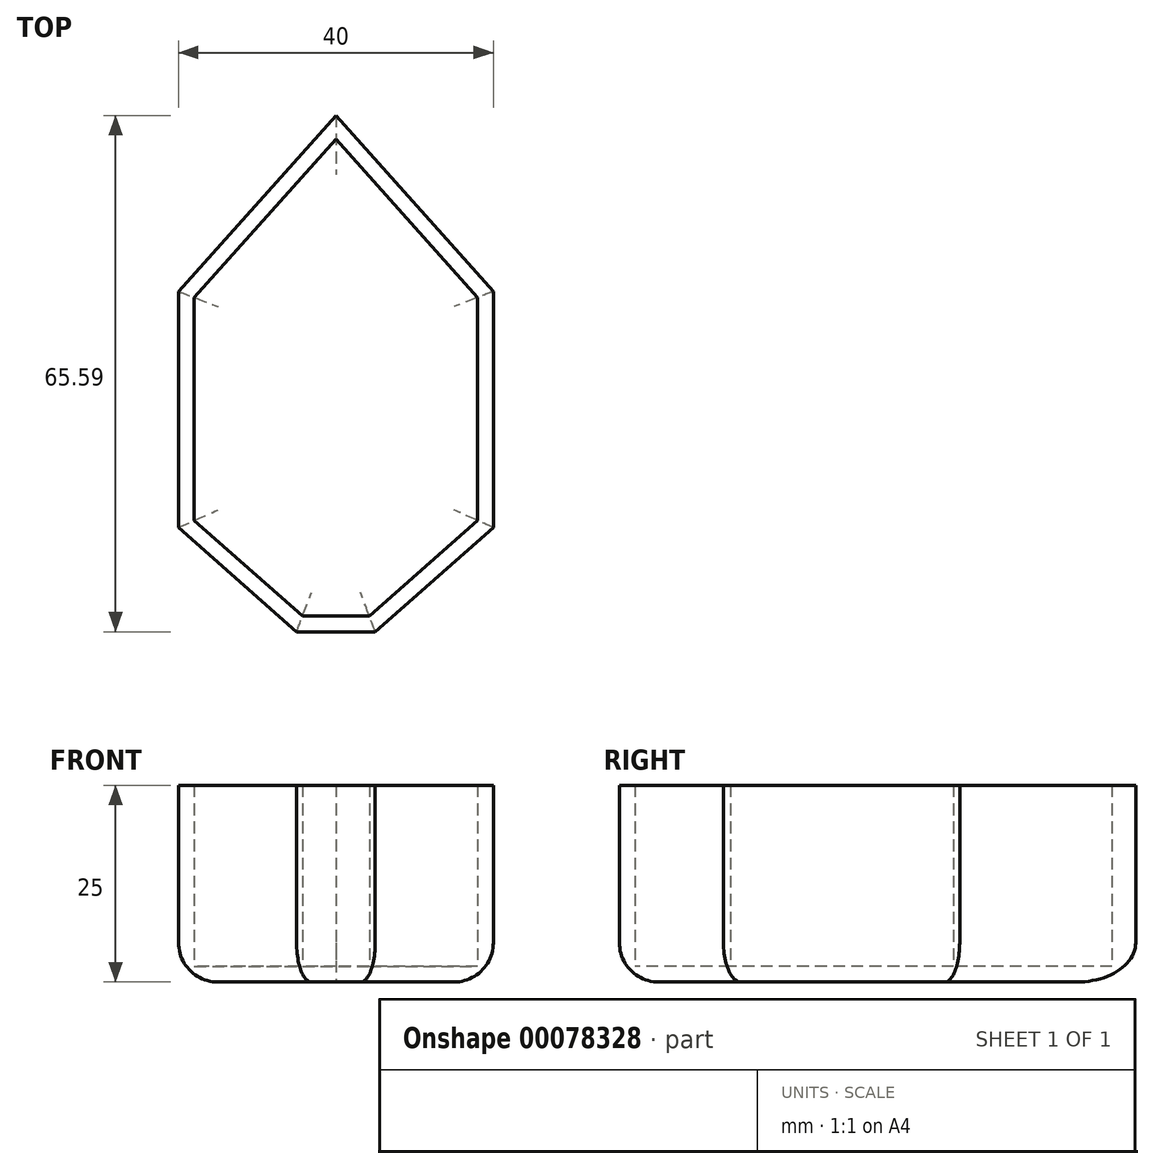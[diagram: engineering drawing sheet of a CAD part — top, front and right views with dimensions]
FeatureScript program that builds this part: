
annotation { "Feature Type Name" : "Feature", "Feature Type Description" : "" }
export const myFeature = defineFeature(function(context is Context, id is Id, definition is map)
    precondition{}
    {
        {
            var Q0;
            Q0=qCreatedBy(makeId("Top.planeOp"),FACE);
            var sketch = newSketch(context, id + "F0", { "sketchPlane" : qUnion([Q0])});
            skLineSegment(sketch, "E0", {"start": v(-20, 52.36) * mm, "end": v(-40, 30) * mm});
            skLineSegment(sketch, "E1", {"start": v(-40, 30) * mm, "end": v(-40, 0) * mm});
            skLineSegment(sketch, "E2", {"start": v(-40, 0) * mm, "end": v(0, 0) * mm});
            skLineSegment(sketch, "E3", {"start": v(0, 0) * mm, "end": v(0, 30) * mm});
            skLineSegment(sketch, "E4", {"start": v(0, 30) * mm, "end": v(-40, 30) * mm});
            skLineSegment(sketch, "E5", {"start": v(0, 30) * mm, "end": v(-20, 52.36) * mm});
            skLineSegment(sketch, "E6", {"start": v(-40, 0) * mm, "end": v(-25, -13.23) * mm});
            skLineSegment(sketch, "E7", {"start": v(-25, -13.23) * mm, "end": v(-15, -13.23) * mm});
            skLineSegment(sketch, "E8", {"start": v(-15, -13.23) * mm, "end": v(0, 0) * mm});
            skSolve(sketch);
        }
        {
            var Q0;
            Q0 = qSketchRegion(id + "F0", true);
            extrude(context, id + "F1", {"entities" : qUnion([Q0]), "depth" : 25 * mm});
        }
        {
            var Q0;
            Q0=makeQuery(id+"F1.opExtrude","CAP_FACE",FACE,{"disambiguationData":[OSD([sQuery(id+"F0.wireOp",EDGE,"E0"),sQuery(id+"F0.wireOp",EDGE,"E1"),sQuery(id+"F0.wireOp",EDGE,"E3"),sQuery(id+"F0.wireOp",EDGE,"E5"),sQuery(id+"F0.wireOp",EDGE,"E6"),sQuery(id+"F0.wireOp",EDGE,"E7"),sQuery(id+"F0.wireOp",EDGE,"E8")])],"isStart":false});
            shell(context, id + "F2", {"entities" : qUnion([Q0]), "thickness" : 2 * mm});
        }
        {
            var Q0;
            Q0=makeQuery(id+"F1.opExtrude","CAP_EDGE",EDGE,{"disambiguationData":[OSD([sQuery(id+"F0.wireOp",EDGE,"E1")])],"isStart":true});
            var Q1;
            Q1=makeQuery(id+"F1.opExtrude","CAP_EDGE",EDGE,{"disambiguationData":[OSD([sQuery(id+"F0.wireOp",EDGE,"E0")])],"isStart":true});
            var Q2;
            Q2=makeQuery(id+"F1.opExtrude","CAP_EDGE",EDGE,{"disambiguationData":[OSD([sQuery(id+"F0.wireOp",EDGE,"E5")])],"isStart":true});
            var Q3;
            Q3=makeQuery(id+"F1.opExtrude","CAP_EDGE",EDGE,{"disambiguationData":[OSD([sQuery(id+"F0.wireOp",EDGE,"E3")])],"isStart":true});
            var Q4;
            Q4=makeQuery(id+"F1.opExtrude","CAP_EDGE",EDGE,{"disambiguationData":[OSD([sQuery(id+"F0.wireOp",EDGE,"E6")])],"isStart":true});
            var Q5;
            Q5=makeQuery(id+"F1.opExtrude","CAP_EDGE",EDGE,{"disambiguationData":[OSD([sQuery(id+"F0.wireOp",EDGE,"E8")])],"isStart":true});
            var Q6;
            Q6=makeQuery(id+"F1.opExtrude","CAP_EDGE",EDGE,{"disambiguationData":[OSD([sQuery(id+"F0.wireOp",EDGE,"E7")])],"isStart":true});
            fillet(context, id + "F3", {"entities" : qUnion([Q0, Q1, Q2, Q3, Q4, Q5, Q6]), "radius" : 5 * mm, "tangentPropagation" : true, "allowEdgeOverflow" : false});
        }
    });
